# Revit family: Haworth_Compose_Panel_Solid
name_source: partatom
category: Furniture Systems
revit_build: Autodesk Revit 2018 (Build: 20170223_1515(x64)
units: mm (PartAtom-declared; Revit-internal decimal feet)

## family parameters
Always vertical = Yes
Cut with Voids When Loaded = No
OmniClass Number = 23.40.70.14.64.21
OmniClass Title = Systems Furniture
Part Type = Normal
Room Calculation Point = No
Round Connector Dimension = Use Diameter
Shared = No
Work Plane-Based = No

## types (60) — shared parameters
Assembly Code = E2020500
Bottom Trim Width = 1 1/2"
Custom Size = No
Description = Haworth - Compose Panel Solid
Manufacturer = Haworth
Max. Height = 163"
Max. Width = 72"
Min. Height = 25"
Min. Width = 18"
Min/Max Height = 34-74 in. @ 8 in. Increments
Min/Max Width = 18-72 in. @ 6 in. Increments
Model = VZFF
Panel Depth = 1/2"
Raceway Finish = Haworth _ Paint _ Putty
Raceway Panel Depth = 1/2"
Revision Number = 6
Size = Verify Final Dim. w/ Haworth
Sustainability Info = http://media.haworth.com
Top Trim = Yes
Top Trim Adjuster = 1/8"
Top Trim Width = 1/8"
Trim Depth = 3"
Trim Finish = Haworth _ Paint _ Putty
Trim Thin Profile = Yes
URL = http://www.haworth.com
URL - Product = http://www.haworth.com
Warranty = http://www.haworth.com

## per-type parameters (varying)
| type | Actual Height | Actual Width | Height | Panel Width | Raceway Panel Width | Width |
| 34h 18w | 33 7/8" | 18" | 34" | 18" | 18" | 18" |
| 34h 24w | 33 7/8" | 24" | 34" | 24" | 24" | 24" |
| 34h 30w | 33 7/8" | 30" | 34" | 30" | 30" | 30" |
| 34h 36w | 33 7/8" | 36" | 34" | 36" | 36" | 36" |
| 34h 42w | 33 7/8" | 42" | 34" | 42" | 42" | 42" |
| 34h 48w | 33 7/8" | 48" | 34" | 48" | 48" | 48" |
| 34h 54w | 33 7/8" | 54" | 34" | 54" | 54" | 54" |
| 34h 60w | 33 7/8" | 60" | 34" | 60" | 60" | 60" |
| 34h 66w | 33 7/8" | 66" | 34" | 66" | 66" | 66" |
| 34h 72w | 33 7/8" | 72" | 34" | 72" | 72" | 72" |
| 42h 18w | 41 7/8" | 18" | 42" | 18" | 18" | 18" |
| 42h 24w | 41 7/8" | 24" | 42" | 24" | 24" | 24" |
| 42h 30w | 41 7/8" | 30" | 42" | 30" | 30" | 30" |
| 42h 36w | 41 7/8" | 36" | 42" | 36" | 36" | 36" |
| 42h 42w | 41 7/8" | 42" | 42" | 42" | 42" | 42" |
| 42h 48w | 41 7/8" | 48" | 42" | 48" | 48" | 48" |
| 42h 54w | 41 7/8" | 54" | 42" | 54" | 54" | 54" |
| 42h 60w | 41 7/8" | 60" | 42" | 60" | 60" | 60" |
| 42h 66w | 41 7/8" | 66" | 42" | 66" | 66" | 66" |
| 42h 72w | 41 7/8" | 72" | 42" | 72" | 72" | 72" |
| 50h 18w | 49 7/8" | 18" | 50" | 18" | 18" | 18" |
| 50h 24w | 49 7/8" | 24" | 50" | 24" | 24" | 24" |
| 50h 30w | 49 7/8" | 30" | 50" | 30" | 30" | 30" |
| 50h 36w | 49 7/8" | 36" | 50" | 36" | 36" | 36" |
| 50h 42w | 49 7/8" | 42" | 50" | 42" | 42" | 42" |
| 50h 48w | 49 7/8" | 48" | 50" | 48" | 48" | 48" |
| 50h 54w | 49 7/8" | 54" | 50" | 54" | 54" | 54" |
| 50h 60w | 49 7/8" | 60" | 50" | 60" | 60" | 60" |
| 50h 66w | 49 7/8" | 66" | 50" | 66" | 66" | 66" |
| 50h 72w | 49 7/8" | 72" | 50" | 72" | 72" | 72" |
| 58h 18w | 57 7/8" | 18" | 58" | 18" | 18" | 18" |
| 58h 24w | 57 7/8" | 24" | 58" | 24" | 24" | 24" |
| 58h 30w | 57 7/8" | 30" | 58" | 30" | 30" | 30" |
| 58h 36w | 57 7/8" | 36" | 58" | 36" | 36" | 36" |
| 58h 42w | 57 7/8" | 42" | 58" | 42" | 42" | 42" |
| 58h 48w | 57 7/8" | 48" | 58" | 48" | 48" | 48" |
| 58h 54w | 57 7/8" | 54" | 58" | 54" | 54" | 54" |
| 58h 60w | 57 7/8" | 60" | 58" | 60" | 60" | 60" |
| 58h 66w | 57 7/8" | 66" | 58" | 66" | 66" | 66" |
| 58h 72w | 57 7/8" | 72" | 58" | 72" | 72" | 72" |
| 66h 18w | 65 7/8" | 18" | 66" | 18" | 18" | 18" |
| 66h 24w | 65 7/8" | 24" | 66" | 24" | 24" | 24" |
| 66h 30w | 65 7/8" | 30" | 66" | 30" | 30" | 30" |
| 66h 36w | 65 7/8" | 36" | 66" | 36" | 36" | 36" |
| 66h 42w | 65 7/8" | 42" | 66" | 42" | 42" | 42" |
| 66h 48w | 65 7/8" | 48" | 66" | 48" | 48" | 48" |
| 66h 54w | 65 7/8" | 54" | 66" | 54" | 54" | 54" |
| 66h 60w | 65 7/8" | 60" | 66" | 60" | 60" | 60" |
| 66h 66w | 65 7/8" | 66" | 66" | 66" | 66" | 66" |
| 66h 72w | 65 7/8" | 72" | 66" | 72" | 72" | 72" |
| 74h 18w | 73 7/8" | 18" | 74" | 18" | 18" | 18" |
| 74h 24w | 73 7/8" | 24" | 74" | 24" | 24" | 24" |
| 74h 30w | 73 7/8" | 30" | 74" | 30" | 30" | 30" |
| 74h 36w | 73 7/8" | 36" | 74" | 36" | 36" | 36" |
| 74h 42w | 73 7/8" | 42" | 74" | 42" | 42" | 42" |
| 74h 48w | 73 7/8" | 48" | 74" | 48" | 48" | 48" |
| 74h 54w | 73 7/8" | 54" | 74" | 54" | 54" | 54" |
| 74h 60w | 73 7/8" | 60" | 74" | 60" | 60" | 60" |
| 74h 66w | 73 7/8" | 66" | 74" | 66" | 66" | 66" |
| 74h 72w | 73 7/8" | 72" | 74" | 72" | 72" | 72" |

## geometry (parser evidence)
native form markers: Sweep x12
no freeform markers — native parametric forms only
